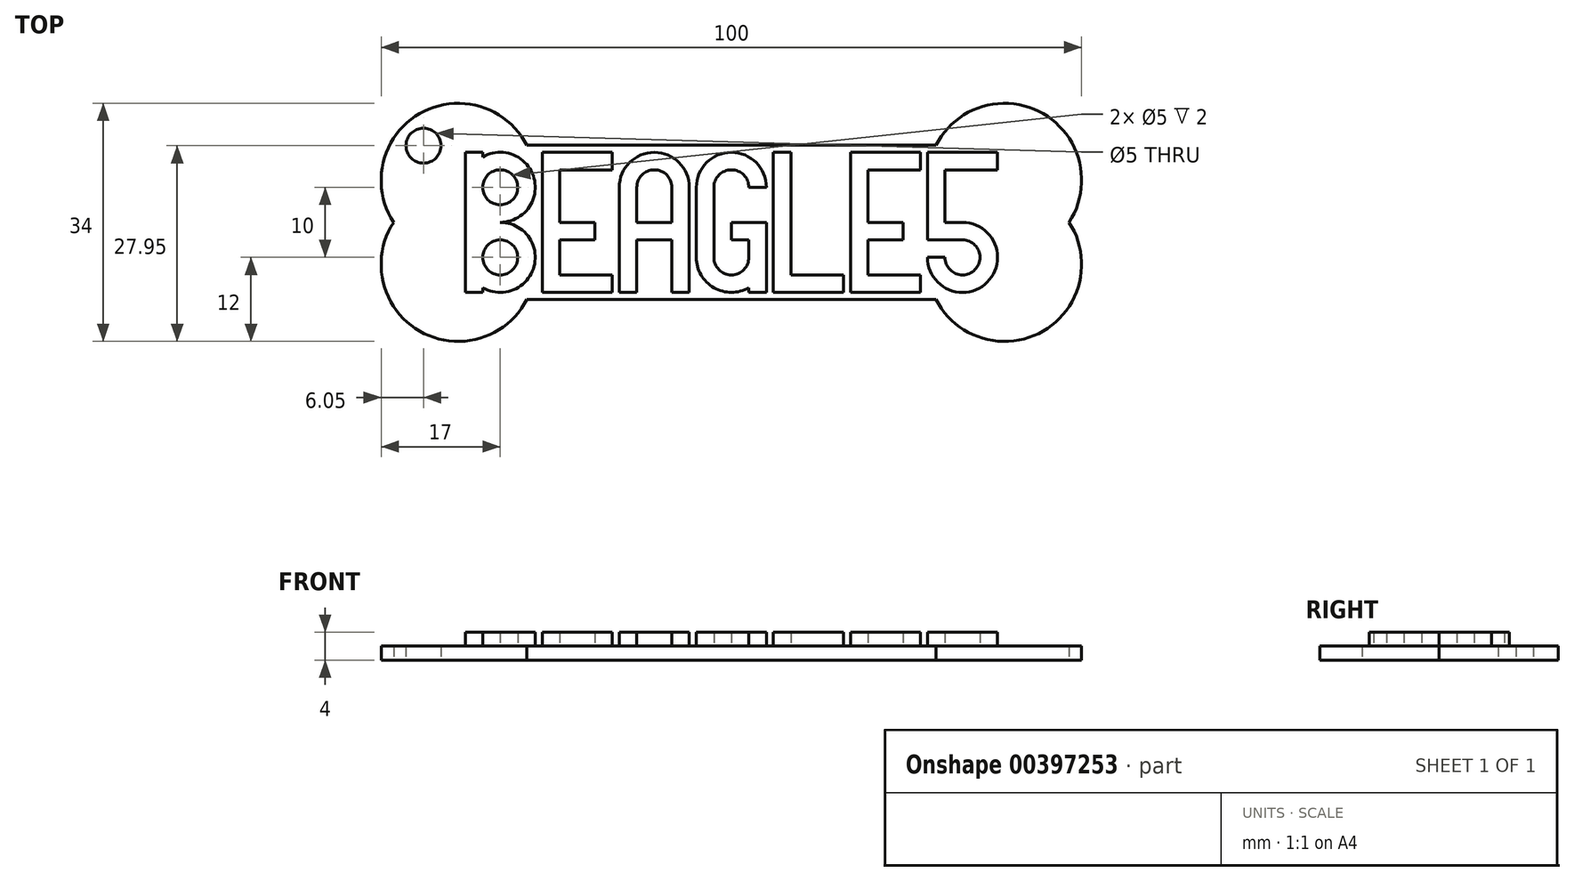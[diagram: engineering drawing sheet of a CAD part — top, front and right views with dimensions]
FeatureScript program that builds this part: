
annotation { "Feature Type Name" : "Feature", "Feature Type Description" : "" }
export const myFeature = defineFeature(function(context is Context, id is Id, definition is map)
    precondition{}
    {
        {
            var Q0;
            Q0=qCreatedBy(makeId("Top.planeOp"),FACE);
            var sketch = newSketch(context, id + "F0", { "sketchPlane" : qUnion([Q0])});
            skLineSegment(sketch, "E0.bottom", {"start": v(0, 0) * mm, "end": v(-78, 0) * mm});
            skLineSegment(sketch, "E0.top", {"start": v(0, 22) * mm, "end": v(-78, 22) * mm});
            skLineSegment(sketch, "E0.left", {"start": v(0, 0) * mm, "end": v(0, 22) * mm});
            skLineSegment(sketch, "E0.right", {"start": v(-78, 0) * mm, "end": v(-78, 22) * mm});
            skPoint(sketch, "E1", {"position": v(-78, 17) * mm});
            skPoint(sketch, "E2", {"position": v(-78, 5) * mm});
            skPoint(sketch, "E3", {"position": v(0, 5) * mm});
            skCircle(sketch, "E4", {"center": v(-78, 17) * mm, "radius": 11 * mm});
            skCircle(sketch, "E5", {"center": v(-78, 5) * mm, "radius": 11 * mm});
            skPoint(sketch, "E6", {"position": v(0, 17) * mm});
            skCircle(sketch, "E7", {"center": v(0, 17) * mm, "radius": 11 * mm});
            skCircle(sketch, "E8", {"center": v(0, 5) * mm, "radius": 11 * mm});
            skLineSegment(sketch, "E9", {"start": v(-78, 17) * mm, "end": v(-89, 17) * mm, "construction": true});
            skLineSegment(sketch, "E10", {"start": v(-78, 17) * mm, "end": v(-85.78, 24.78) * mm, "construction": true});
            skCircle(sketch, "E11", {"center": v(-82.95, 21.95) * mm, "radius": 2.5 * mm});
            skSolve(sketch);
        }
        {
            var Q0;
            Q0 = qSketchRegion(id + "F0", true);
            var Q1;
            {var subQ0=sQuery(id+"F0.wireOp",EDGE,"E4");var subQ1=sQuery(id+"F0.wireOp",EDGE,"E0.right");var subQ2=makeQuery(id+"F0.imprint","INTERSECT",VERTEX,{"derivedFrom":[subQ1,subQ0]});Q1=makeQuery(id+"F0.imprint","IMPRINT",FACE,{"disambiguationData":[TD([[makeQuery(id+"F0.imprint","IMPRINT",EDGE,{"disambiguationData":[TD([[subQ2,-1.0]])],"derivedFrom":subQ1}),-1.0]])]});}
            var Q2;
            {var subQ0=sQuery(id+"F0.wireOp",EDGE,"E7");var subQ1=sQuery(id+"F0.wireOp",EDGE,"E0.left");var subQ2=makeQuery(id+"F0.imprint","INTERSECT",VERTEX,{"derivedFrom":[subQ1,subQ0]});Q2=makeQuery(id+"F0.imprint","IMPRINT",FACE,{"disambiguationData":[TD([[makeQuery(id+"F0.imprint","IMPRINT",EDGE,{"disambiguationData":[TD([[subQ2,-1.0]])],"derivedFrom":subQ1}),1.0]])]});}
            extrude(context, id + "F1", {"entities" : qUnion([Q0, Q1, Q2]), "depth" : 2 * mm});
        }
        {
            var Q0;
            Q0=makeQuery(id+"F1.opExtrude","CAP_FACE",FACE,{"disambiguationData":[OSD([sQuery(id+"F0.wireOp",EDGE,"E0.bottom"),sQuery(id+"F0.wireOp",EDGE,"E0.top"),sQuery(id+"F0.wireOp",EDGE,"E4"),sQuery(id+"F0.wireOp",EDGE,"E5"),sQuery(id+"F0.wireOp",EDGE,"E7"),sQuery(id+"F0.wireOp",EDGE,"E8"),sQuery(id+"F0.wireOp",EDGE,"E11")])],"isStart":false});
            var sketch = newSketch(context, id + "F2", { "sketchPlane" : qUnion([Q0])});
            skLineSegment(sketch, "E12.bottom", {"start": v(0, 0) * mm, "end": v(-78, 0) * mm, "construction": true});
            skLineSegment(sketch, "E12.top", {"start": v(0, 22) * mm, "end": v(-78, 22) * mm, "construction": true});
            skLineSegment(sketch, "E12.left", {"start": v(0, 0) * mm, "end": v(0, 22) * mm, "construction": true});
            skLineSegment(sketch, "E12.right", {"start": v(-78, 0) * mm, "end": v(-78, 22) * mm, "construction": true});
            skLineSegment(sketch, "E13.bottom", {"start": v(-77, 21) * mm, "end": v(-67, 21) * mm, "construction": true});
            skLineSegment(sketch, "E13.top", {"start": v(-77, 1) * mm, "end": v(-67, 1) * mm, "construction": true});
            skLineSegment(sketch, "E13.left", {"start": v(-77, 21) * mm, "end": v(-77, 1) * mm, "construction": true});
            skLineSegment(sketch, "E13.right", {"start": v(-67, 21) * mm, "end": v(-67, 1) * mm, "construction": true});
            skLineSegment(sketch, "E14", {"start": v(-77, 11) * mm, "end": v(-67, 11) * mm, "construction": true});
            skLineSegment(sketch, "E15.bottom", {"start": v(-22, 21) * mm, "end": v(-12, 21) * mm, "construction": true});
            skLineSegment(sketch, "E15.top", {"start": v(-22, 1) * mm, "end": v(-12, 1) * mm, "construction": true});
            skLineSegment(sketch, "E15.left", {"start": v(-22, 21) * mm, "end": v(-22, 1) * mm, "construction": true});
            skLineSegment(sketch, "E15.right", {"start": v(-12, 21) * mm, "end": v(-12, 1) * mm, "construction": true});
            skLineSegment(sketch, "E16", {"start": v(-22, 11) * mm, "end": v(-12, 11) * mm, "construction": true});
            skLineSegment(sketch, "E17.bottom", {"start": v(-55, 21) * mm, "end": v(-45, 21) * mm, "construction": true});
            skLineSegment(sketch, "E17.top", {"start": v(-55, 1) * mm, "end": v(-45, 1) * mm, "construction": true});
            skLineSegment(sketch, "E17.left", {"start": v(-55, 21) * mm, "end": v(-55, 1) * mm, "construction": true});
            skLineSegment(sketch, "E17.right", {"start": v(-45, 21) * mm, "end": v(-45, 1) * mm, "construction": true});
            skLineSegment(sketch, "E18", {"start": v(-55, 11) * mm, "end": v(-45, 11) * mm, "construction": true});
            skLineSegment(sketch, "E19.bottom", {"start": v(-33, 21) * mm, "end": v(-23, 21) * mm, "construction": true});
            skLineSegment(sketch, "E19.top", {"start": v(-33, 1) * mm, "end": v(-23, 1) * mm, "construction": true});
            skLineSegment(sketch, "E19.left", {"start": v(-33, 21) * mm, "end": v(-33, 1) * mm, "construction": true});
            skLineSegment(sketch, "E19.right", {"start": v(-23, 21) * mm, "end": v(-23, 1) * mm, "construction": true});
            skLineSegment(sketch, "E20", {"start": v(-28, 21) * mm, "end": v(-28, 1) * mm, "construction": true});
            skLineSegment(sketch, "E21", {"start": v(-33, 11) * mm, "end": v(-23, 11) * mm, "construction": true});
            skLineSegment(sketch, "E22.bottom", {"start": v(-11, 21) * mm, "end": v(-1, 21) * mm, "construction": true});
            skLineSegment(sketch, "E22.top", {"start": v(-11, 1) * mm, "end": v(-1, 1) * mm, "construction": true});
            skLineSegment(sketch, "E22.left", {"start": v(-11, 21) * mm, "end": v(-11, 1) * mm, "construction": true});
            skLineSegment(sketch, "E22.right", {"start": v(-1, 21) * mm, "end": v(-1, 1) * mm, "construction": true});
            skLineSegment(sketch, "E23", {"start": v(-6, 21) * mm, "end": v(-6, 1) * mm, "construction": true});
            skLineSegment(sketch, "E24", {"start": v(-11, 11) * mm, "end": v(-1, 11) * mm, "construction": true});
            skLineSegment(sketch, "E25", {"start": v(-77, 21) * mm, "end": v(-67, 11) * mm, "construction": true});
            skLineSegment(sketch, "E26", {"start": v(-77, 11) * mm, "end": v(-67, 21) * mm, "construction": true});
            skLineSegment(sketch, "E27", {"start": v(-77, 11) * mm, "end": v(-67, 1) * mm, "construction": true});
            skLineSegment(sketch, "E28", {"start": v(-77, 1) * mm, "end": v(-67, 11) * mm, "construction": true});
            skCircle(sketch, "E29", {"center": v(-72, 16) * mm, "radius": 5 * mm});
            skCircle(sketch, "E30", {"center": v(-72, 6) * mm, "radius": 5 * mm});
            skLineSegment(sketch, "E31", {"start": v(-74.5, 21) * mm, "end": v(-74.5, 1) * mm});
            skCircle(sketch, "E32", {"center": v(-72, 16) * mm, "radius": 2.5 * mm});
            skCircle(sketch, "E33", {"center": v(-72, 6) * mm, "radius": 2.5 * mm});
            skLineSegment(sketch, "E34", {"start": v(-77, 21) * mm, "end": v(-74.5, 21) * mm});
            skLineSegment(sketch, "E35", {"start": v(-77, 21) * mm, "end": v(-77, 1) * mm});
            skLineSegment(sketch, "E36", {"start": v(-77, 1) * mm, "end": v(-74.5, 1) * mm});
            skLineSegment(sketch, "E37", {"start": v(-22, 21) * mm, "end": v(-22, 1) * mm});
            skLineSegment(sketch, "E38", {"start": v(-19.5, 1) * mm, "end": v(-19.5, 21) * mm});
            skLineSegment(sketch, "E39", {"start": v(-22, 18.5) * mm, "end": v(-12, 18.5) * mm});
            skLineSegment(sketch, "E40", {"start": v(-22, 3.5) * mm, "end": v(-12, 3.5) * mm});
            skLineSegment(sketch, "E41", {"start": v(-22, 11) * mm, "end": v(-12, 11) * mm});
            skLineSegment(sketch, "E42", {"start": v(-22, 8.5) * mm, "end": v(-12, 8.5) * mm});
            skLineSegment(sketch, "E43", {"start": v(-14.5, 11) * mm, "end": v(-14.5, 8.5) * mm});
            skLineSegment(sketch, "E44", {"start": v(-22, 21) * mm, "end": v(-12, 21) * mm});
            skLineSegment(sketch, "E45", {"start": v(-22, 1) * mm, "end": v(-12, 1) * mm});
            skLineSegment(sketch, "E46", {"start": v(-12, 21) * mm, "end": v(-12, 18.5) * mm});
            skLineSegment(sketch, "E47", {"start": v(-12, 3.5) * mm, "end": v(-12, 1) * mm});
            skLineSegment(sketch, "E48", {"start": v(-55, 21) * mm, "end": v(-45, 11) * mm, "construction": true});
            skLineSegment(sketch, "E49", {"start": v(-45, 21) * mm, "end": v(-55, 11) * mm, "construction": true});
            skLineSegment(sketch, "E50", {"start": v(-55, 21) * mm, "end": v(-55, 1) * mm});
            skLineSegment(sketch, "E51", {"start": v(-45, 21) * mm, "end": v(-45, 1) * mm});
            skLineSegment(sketch, "E52", {"start": v(-55, 11) * mm, "end": v(-45, 11) * mm});
            skLineSegment(sketch, "E53", {"start": v(-55, 8.5) * mm, "end": v(-45, 8.5) * mm});
            skLineSegment(sketch, "E54", {"start": v(-52.5, 21) * mm, "end": v(-52.5, 1) * mm});
            skLineSegment(sketch, "E55", {"start": v(-47.5, 21) * mm, "end": v(-47.5, 1) * mm});
            skLineSegment(sketch, "E56", {"start": v(-55, 1) * mm, "end": v(-52.5, 1) * mm});
            skLineSegment(sketch, "E57", {"start": v(-47.5, 1) * mm, "end": v(-45, 1) * mm});
            skCircle(sketch, "E58", {"center": v(-50, 16) * mm, "radius": 5 * mm});
            skCircle(sketch, "E59", {"center": v(-50, 16) * mm, "radius": 2.5 * mm});
            skLineSegment(sketch, "E60", {"start": v(-30.5, 21) * mm, "end": v(-30.5, 1) * mm});
            skLineSegment(sketch, "E61", {"start": v(-33, 21) * mm, "end": v(-33, 1) * mm});
            skLineSegment(sketch, "E62", {"start": v(-33, 21) * mm, "end": v(-30.5, 21) * mm});
            skLineSegment(sketch, "E63", {"start": v(-33, 1) * mm, "end": v(-30.5, 1) * mm});
            skLineSegment(sketch, "E64", {"start": v(-33, 3.5) * mm, "end": v(-23, 3.5) * mm});
            skLineSegment(sketch, "E65", {"start": v(-23, 3.5) * mm, "end": v(-23, 1) * mm});
            skLineSegment(sketch, "E66", {"start": v(-33, 1) * mm, "end": v(-23, 1) * mm});
            skLineSegment(sketch, "E67", {"start": v(-11, 21) * mm, "end": v(-1, 21) * mm});
            skLineSegment(sketch, "E68", {"start": v(-11, 21) * mm, "end": v(-11, 1) * mm});
            skLineSegment(sketch, "E69", {"start": v(-11, 11) * mm, "end": v(-1, 11) * mm});
            skLineSegment(sketch, "E70", {"start": v(-11, 11) * mm, "end": v(-1, 1) * mm, "construction": true});
            skLineSegment(sketch, "E71", {"start": v(-1, 11) * mm, "end": v(-11, 1) * mm, "construction": true});
            skCircle(sketch, "E72", {"center": v(-6, 6) * mm, "radius": 5 * mm});
            skLineSegment(sketch, "E73.bottom", {"start": v(-66, 21) * mm, "end": v(-56, 21) * mm, "construction": true});
            skLineSegment(sketch, "E73.top", {"start": v(-66, 1) * mm, "end": v(-56, 1) * mm, "construction": true});
            skLineSegment(sketch, "E73.left", {"start": v(-66, 21) * mm, "end": v(-66, 1) * mm, "construction": true});
            skLineSegment(sketch, "E73.right", {"start": v(-56, 21) * mm, "end": v(-56, 1) * mm, "construction": true});
            skLineSegment(sketch, "E74", {"start": v(-66, 11) * mm, "end": v(-56, 11) * mm, "construction": true});
            skLineSegment(sketch, "E75", {"start": v(-66, 21) * mm, "end": v(-66, 1) * mm});
            skLineSegment(sketch, "E76", {"start": v(-63.5, 1) * mm, "end": v(-63.5, 21) * mm});
            skLineSegment(sketch, "E77", {"start": v(-66, 18.5) * mm, "end": v(-56, 18.5) * mm});
            skLineSegment(sketch, "E78", {"start": v(-66, 3.5) * mm, "end": v(-56, 3.5) * mm});
            skLineSegment(sketch, "E79", {"start": v(-66, 11) * mm, "end": v(-56, 11) * mm});
            skLineSegment(sketch, "E80", {"start": v(-66, 8.5) * mm, "end": v(-56, 8.5) * mm});
            skLineSegment(sketch, "E81", {"start": v(-58.5, 11) * mm, "end": v(-58.5, 8.5) * mm});
            skLineSegment(sketch, "E82", {"start": v(-66, 21) * mm, "end": v(-56, 21) * mm});
            skLineSegment(sketch, "E83", {"start": v(-66, 1) * mm, "end": v(-56, 1) * mm});
            skLineSegment(sketch, "E84", {"start": v(-56, 21) * mm, "end": v(-56, 18.5) * mm});
            skLineSegment(sketch, "E85", {"start": v(-56, 3.5) * mm, "end": v(-56, 1) * mm});
            skLineSegment(sketch, "E86.bottom", {"start": v(-44, 21) * mm, "end": v(-34, 21) * mm, "construction": true});
            skLineSegment(sketch, "E86.top", {"start": v(-44, 1) * mm, "end": v(-34, 1) * mm, "construction": true});
            skLineSegment(sketch, "E86.left", {"start": v(-44, 21) * mm, "end": v(-44, 1) * mm, "construction": true});
            skLineSegment(sketch, "E86.right", {"start": v(-34, 21) * mm, "end": v(-34, 1) * mm, "construction": true});
            skLineSegment(sketch, "E87", {"start": v(-44, 11) * mm, "end": v(-34, 11) * mm, "construction": true});
            skLineSegment(sketch, "E88", {"start": v(-44, 21) * mm, "end": v(-34, 11) * mm, "construction": true});
            skLineSegment(sketch, "E89", {"start": v(-44, 11) * mm, "end": v(-34, 21) * mm, "construction": true});
            skLineSegment(sketch, "E90", {"start": v(-44, 11) * mm, "end": v(-34, 1) * mm, "construction": true});
            skLineSegment(sketch, "E91", {"start": v(-44, 1) * mm, "end": v(-34, 11) * mm, "construction": true});
            skCircle(sketch, "E92", {"center": v(-39, 16) * mm, "radius": 5 * mm});
            skCircle(sketch, "E93", {"center": v(-39, 6) * mm, "radius": 5 * mm});
            skLineSegment(sketch, "E94", {"start": v(-41.5, 21) * mm, "end": v(-41.5, 1) * mm});
            skCircle(sketch, "E95", {"center": v(-39, 6) * mm, "radius": 2.5 * mm});
            skLineSegment(sketch, "E96", {"start": v(-44, 21) * mm, "end": v(-41.5, 21) * mm});
            skLineSegment(sketch, "E97", {"start": v(-44, 21) * mm, "end": v(-44, 1) * mm});
            skLineSegment(sketch, "E98", {"start": v(-44, 1) * mm, "end": v(-41.5, 1) * mm});
            skLineSegment(sketch, "E99", {"start": v(-36.5, 21) * mm, "end": v(-36.5, 1) * mm});
            skLineSegment(sketch, "E100", {"start": v(-34, 11) * mm, "end": v(-34, 1) * mm});
            skLineSegment(sketch, "E101", {"start": v(-36.5, 11) * mm, "end": v(-34, 11) * mm});
            skLineSegment(sketch, "E102", {"start": v(-44, 11) * mm, "end": v(-34, 11) * mm});
            skLineSegment(sketch, "E103", {"start": v(-44, 8.5) * mm, "end": v(-34, 8.5) * mm});
            skCircle(sketch, "E104", {"center": v(-39, 16) * mm, "radius": 2.5 * mm});
            skLineSegment(sketch, "E105", {"start": v(-36.5, 16) * mm, "end": v(-34, 16) * mm});
            skLineSegment(sketch, "E106", {"start": v(-36.5, 1) * mm, "end": v(-34, 1) * mm});
            skLineSegment(sketch, "E107", {"start": v(-39, 8.5) * mm, "end": v(-39, 11) * mm});
            skLineSegment(sketch, "E108", {"start": v(-1, 18.5) * mm, "end": v(-11, 18.5) * mm});
            skLineSegment(sketch, "E109", {"start": v(-1, 21) * mm, "end": v(-1, 18.5) * mm});
            skLineSegment(sketch, "E110", {"start": v(-8.5, 21) * mm, "end": v(-8.5, 11) * mm});
            skLineSegment(sketch, "E111", {"start": v(-11, 8.5) * mm, "end": v(-1, 8.5) * mm});
            skCircle(sketch, "E112", {"center": v(-6, 6) * mm, "radius": 2.5 * mm});
            skLineSegment(sketch, "E113", {"start": v(-8.5, 6) * mm, "end": v(-11, 6) * mm});
            skSolve(sketch);
        }
        {
            var Q0;
            {var subQ0=sQuery(id+"F2.wireOp",EDGE,"E109");Q0=makeQuery(id+"F2.imprint","IMPRINT",FACE,{"disambiguationData":[TD([[makeQuery(id+"F2.imprint","IMPRINT",EDGE,{"derivedFrom":subQ0}),-1.0]])]});}
            var Q1;
            {var subQ0=sQuery(id+"F2.wireOp",EDGE,"E68");var subQ1=sQuery(id+"F2.wireOp",EDGE,"E67");var subQ2=makeQuery(id+"F2.imprint","INTERSECT",VERTEX,{"derivedFrom":[subQ1,subQ0]});Q1=makeQuery(id+"F2.imprint","IMPRINT",FACE,{"disambiguationData":[TD([[makeQuery(id+"F2.imprint","IMPRINT",EDGE,{"disambiguationData":[TD([[subQ2,-1.0]])],"derivedFrom":subQ1}),-1.0]])]});}
            var Q2;
            {var subQ0=sQuery(id+"F2.wireOp",EDGE,"E69");var subQ1=sQuery(id+"F2.wireOp",EDGE,"E68");var subQ2=makeQuery(id+"F2.imprint","INTERSECT",VERTEX,{"derivedFrom":[subQ1,subQ0]});Q2=makeQuery(id+"F2.imprint","IMPRINT",FACE,{"disambiguationData":[TD([[makeQuery(id+"F2.imprint","IMPRINT",EDGE,{"disambiguationData":[TD([[subQ2,1.0]])],"derivedFrom":subQ1}),1.0]])]});}
            var Q3;
            {var subQ0=sQuery(id+"F2.wireOp",EDGE,"E69");var subQ4=sQuery(id+"F2.wireOp",EDGE,"E68");var subQ5=makeQuery(id+"F2.imprint","INTERSECT",VERTEX,{"derivedFrom":[subQ4,subQ0]});Q3=makeQuery(id+"F2.imprint","IMPRINT",FACE,{"disambiguationData":[TD([[makeQuery(id+"F2.imprint","IMPRINT",EDGE,{"disambiguationData":[TD([[subQ5,-1.0]])],"derivedFrom":subQ4}),1.0]])]});}
            var Q4;
            {var subQ0=sQuery(id+"F2.wireOp",EDGE,"E72");var subQ1=makeQuery(id+"F2.imprint","INTERSECT",VERTEX,{"derivedFrom":[sQuery(id+"F2.wireOp",EDGE,"E69"),subQ0]});Q4=makeQuery(id+"F2.imprint","IMPRINT",FACE,{"disambiguationData":[TD([[makeQuery(id+"F2.imprint","IMPRINT",EDGE,{"disambiguationData":[TD([[subQ1,1.0]])],"derivedFrom":subQ0}),1.0]])]});}
            var Q5;
            {var subQ0=sQuery(id+"F2.wireOp",EDGE,"E113");Q5=makeQuery(id+"F2.imprint","IMPRINT",FACE,{"disambiguationData":[TD([[makeQuery(id+"F2.imprint","IMPRINT",EDGE,{"derivedFrom":subQ0}),1.0]])]});}
            var Q6;
            {var subQ5=sQuery(id+"F2.wireOp",EDGE,"E43");Q6=makeQuery(id+"F2.imprint","IMPRINT",FACE,{"disambiguationData":[TD([[makeQuery(id+"F2.imprint","IMPRINT",EDGE,{"derivedFrom":subQ5}),-1.0]])]});}
            var Q7;
            {var subQ0=sQuery(id+"F2.wireOp",EDGE,"E41");var subQ1=sQuery(id+"F2.wireOp",EDGE,"E37");var subQ2=makeQuery(id+"F2.imprint","INTERSECT",VERTEX,{"derivedFrom":[subQ1,subQ0]});Q7=makeQuery(id+"F2.imprint","IMPRINT",FACE,{"disambiguationData":[TD([[makeQuery(id+"F2.imprint","IMPRINT",EDGE,{"disambiguationData":[TD([[subQ2,-1.0]])],"derivedFrom":subQ1}),1.0]])]});}
            var Q8;
            {var subQ0=sQuery(id+"F2.wireOp",EDGE,"E39");var subQ1=sQuery(id+"F2.wireOp",EDGE,"E37");var subQ2=makeQuery(id+"F2.imprint","INTERSECT",VERTEX,{"derivedFrom":[subQ1,subQ0]});Q8=makeQuery(id+"F2.imprint","IMPRINT",FACE,{"disambiguationData":[TD([[makeQuery(id+"F2.imprint","IMPRINT",EDGE,{"disambiguationData":[TD([[subQ2,-1.0]])],"derivedFrom":subQ1}),1.0]])]});}
            var Q9;
            {var subQ0=sQuery(id+"F2.wireOp",EDGE,"E44");var subQ1=sQuery(id+"F2.wireOp",EDGE,"E37");var subQ2=makeQuery(id+"F2.imprint","INTERSECT",VERTEX,{"derivedFrom":[subQ1,subQ0]});Q9=makeQuery(id+"F2.imprint","IMPRINT",FACE,{"disambiguationData":[TD([[makeQuery(id+"F2.imprint","IMPRINT",EDGE,{"disambiguationData":[TD([[subQ2,-1.0]])],"derivedFrom":subQ1}),1.0]])]});}
            var Q10;
            {var subQ5=sQuery(id+"F2.wireOp",EDGE,"E46");Q10=makeQuery(id+"F2.imprint","IMPRINT",FACE,{"disambiguationData":[TD([[makeQuery(id+"F2.imprint","IMPRINT",EDGE,{"derivedFrom":subQ5}),-1.0]])]});}
            var Q11;
            {var subQ0=sQuery(id+"F2.wireOp",EDGE,"E40");var subQ1=sQuery(id+"F2.wireOp",EDGE,"E37");var subQ2=makeQuery(id+"F2.imprint","INTERSECT",VERTEX,{"derivedFrom":[subQ1,subQ0]});Q11=makeQuery(id+"F2.imprint","IMPRINT",FACE,{"disambiguationData":[TD([[makeQuery(id+"F2.imprint","IMPRINT",EDGE,{"disambiguationData":[TD([[subQ2,1.0]])],"derivedFrom":subQ1}),1.0]])]});}
            var Q12;
            {var subQ0=sQuery(id+"F2.wireOp",EDGE,"E45");var subQ1=sQuery(id+"F2.wireOp",EDGE,"E37");var subQ2=makeQuery(id+"F2.imprint","INTERSECT",VERTEX,{"derivedFrom":[subQ1,subQ0]});Q12=makeQuery(id+"F2.imprint","IMPRINT",FACE,{"disambiguationData":[TD([[makeQuery(id+"F2.imprint","IMPRINT",EDGE,{"disambiguationData":[TD([[subQ2,1.0]])],"derivedFrom":subQ1}),1.0]])]});}
            var Q13;
            {var subQ5=sQuery(id+"F2.wireOp",EDGE,"E47");Q13=makeQuery(id+"F2.imprint","IMPRINT",FACE,{"disambiguationData":[TD([[makeQuery(id+"F2.imprint","IMPRINT",EDGE,{"derivedFrom":subQ5}),-1.0]])]});}
            var Q14;
            {var subQ5=sQuery(id+"F2.wireOp",EDGE,"E65");Q14=makeQuery(id+"F2.imprint","IMPRINT",FACE,{"disambiguationData":[TD([[makeQuery(id+"F2.imprint","IMPRINT",EDGE,{"derivedFrom":subQ5}),-1.0]])]});}
            var Q15;
            {var subQ0=sQuery(id+"F2.wireOp",EDGE,"E66");var subQ1=sQuery(id+"F2.wireOp",EDGE,"E60");var subQ2=makeQuery(id+"F2.imprint","INTERSECT",VERTEX,{"derivedFrom":[subQ1,subQ0]});Q15=makeQuery(id+"F2.imprint","IMPRINT",FACE,{"disambiguationData":[TD([[makeQuery(id+"F2.imprint","IMPRINT",EDGE,{"disambiguationData":[TD([[subQ2,1.0]])],"derivedFrom":subQ1}),-1.0]])]});}
            var Q16;
            {var subQ0=sQuery(id+"F2.wireOp",EDGE,"E62");Q16=makeQuery(id+"F2.imprint","IMPRINT",FACE,{"disambiguationData":[TD([[makeQuery(id+"F2.imprint","IMPRINT",EDGE,{"derivedFrom":subQ0}),-1.0]])]});}
            var Q17;
            {var subQ0=sQuery(id+"F2.wireOp",EDGE,"E94");var subQ1=sQuery(id+"F2.wireOp",EDGE,"E92");var subQ2=makeQuery(id+"F2.imprint","INTERSECT",VERTEX,{"disambiguationData":[OD(0.0)],"derivedFrom":[subQ1,subQ0]});Q17=makeQuery(id+"F2.imprint","IMPRINT",FACE,{"disambiguationData":[TD([[makeQuery(id+"F2.imprint","IMPRINT",EDGE,{"disambiguationData":[TD([[subQ2,-1.0]])],"derivedFrom":subQ1}),1.0]])]});}
            var Q18;
            {var subQ0=sQuery(id+"F2.wireOp",EDGE,"E97");var subQ1=sQuery(id+"F2.wireOp",EDGE,"E92");var subQ2=makeQuery(id+"F2.imprint","INTERSECT",VERTEX,{"derivedFrom":[subQ1,subQ0]});Q18=makeQuery(id+"F2.imprint","IMPRINT",FACE,{"disambiguationData":[TD([[makeQuery(id+"F2.imprint","IMPRINT",EDGE,{"disambiguationData":[TD([[subQ2,-1.0]])],"derivedFrom":subQ1}),-1.0]])]});}
            var Q19;
            {var subQ0=sQuery(id+"F2.wireOp",EDGE,"E94");var subQ1=sQuery(id+"F2.wireOp",EDGE,"E93");var subQ2=makeQuery(id+"F2.imprint","INTERSECT",VERTEX,{"disambiguationData":[OD(0.0)],"derivedFrom":[subQ1,subQ0]});Q19=makeQuery(id+"F2.imprint","IMPRINT",FACE,{"disambiguationData":[TD([[makeQuery(id+"F2.imprint","IMPRINT",EDGE,{"disambiguationData":[TD([[subQ2,-1.0]])],"derivedFrom":subQ1}),-1.0]])]});}
            var Q20;
            {var subQ1=sQuery(id+"F2.wireOp",EDGE,"E93");var subQ4=sQuery(id+"F2.wireOp",EDGE,"E103");var subQ5=makeQuery(id+"F2.imprint","INTERSECT",VERTEX,{"disambiguationData":[OD(1.0)],"derivedFrom":[subQ1,subQ4]});Q20=makeQuery(id+"F2.imprint","IMPRINT",FACE,{"disambiguationData":[TD([[makeQuery(id+"F2.imprint","IMPRINT",EDGE,{"disambiguationData":[TD([[subQ5,-1.0]])],"derivedFrom":subQ1}),1.0]])]});}
            var Q21;
            {var subQ0=sQuery(id+"F2.wireOp",EDGE,"E103");var subQ1=sQuery(id+"F2.wireOp",EDGE,"E93");var subQ2=makeQuery(id+"F2.imprint","INTERSECT",VERTEX,{"disambiguationData":[OD(1.0)],"derivedFrom":[subQ1,subQ0]});Q21=makeQuery(id+"F2.imprint","IMPRINT",FACE,{"disambiguationData":[TD([[makeQuery(id+"F2.imprint","IMPRINT",EDGE,{"disambiguationData":[TD([[subQ2,-1.0]])],"derivedFrom":subQ1}),-1.0]])]});}
            var Q22;
            {var subQ0=sQuery(id+"F2.wireOp",EDGE,"E94");var subQ1=sQuery(id+"F2.wireOp",EDGE,"E93");var subQ2=makeQuery(id+"F2.imprint","INTERSECT",VERTEX,{"disambiguationData":[OD(0.0)],"derivedFrom":[subQ1,subQ0]});Q22=makeQuery(id+"F2.imprint","IMPRINT",FACE,{"disambiguationData":[TD([[makeQuery(id+"F2.imprint","IMPRINT",EDGE,{"disambiguationData":[TD([[subQ2,-1.0]])],"derivedFrom":subQ1}),1.0]])]});}
            var Q23;
            {var subQ0=sQuery(id+"F2.wireOp",EDGE,"E107");Q23=makeQuery(id+"F2.imprint","IMPRINT",FACE,{"disambiguationData":[TD([[makeQuery(id+"F2.imprint","IMPRINT",EDGE,{"derivedFrom":subQ0}),-1.0]])]});}
            var Q24;
            {var subQ1=sQuery(id+"F2.wireOp",EDGE,"E93");var subQ3=sQuery(id+"F2.wireOp",EDGE,"E99");var subQ4=makeQuery(id+"F2.imprint","INTERSECT",VERTEX,{"disambiguationData":[OD(0.0)],"derivedFrom":[subQ1,subQ3]});Q24=makeQuery(id+"F2.imprint","IMPRINT",FACE,{"disambiguationData":[TD([[makeQuery(id+"F2.imprint","IMPRINT",EDGE,{"disambiguationData":[TD([[subQ4,1.0]])],"derivedFrom":subQ3}),-1.0]])]});}
            var Q25;
            {var subQ5=sQuery(id+"F2.wireOp",EDGE,"E93");var subQ7=sQuery(id+"F2.wireOp",EDGE,"E103");var subQ9=makeQuery(id+"F2.imprint","INTERSECT",VERTEX,{"disambiguationData":[OD(0.0)],"derivedFrom":[subQ5,subQ7]});Q25=makeQuery(id+"F2.imprint","IMPRINT",FACE,{"disambiguationData":[TD([[makeQuery(id+"F2.imprint","IMPRINT",EDGE,{"disambiguationData":[TD([[subQ9,-1.0]])],"derivedFrom":subQ5}),-1.0]])]});}
            var Q26;
            {var subQ0=sQuery(id+"F2.wireOp",EDGE,"E103");var subQ1=sQuery(id+"F2.wireOp",EDGE,"E93");var subQ2=makeQuery(id+"F2.imprint","INTERSECT",VERTEX,{"disambiguationData":[OD(0.0)],"derivedFrom":[subQ1,subQ0]});Q26=makeQuery(id+"F2.imprint","IMPRINT",FACE,{"disambiguationData":[TD([[makeQuery(id+"F2.imprint","IMPRINT",EDGE,{"disambiguationData":[TD([[subQ2,-1.0]])],"derivedFrom":subQ1}),1.0]])]});}
            var Q27;
            {var subQ1=sQuery(id+"F2.wireOp",EDGE,"E93");var subQ4=sQuery(id+"F2.wireOp",EDGE,"E103");var subQ6=makeQuery(id+"F2.imprint","INTERSECT",VERTEX,{"disambiguationData":[OD(0.0)],"derivedFrom":[subQ1,subQ4]});Q27=makeQuery(id+"F2.imprint","IMPRINT",FACE,{"disambiguationData":[TD([[makeQuery(id+"F2.imprint","IMPRINT",EDGE,{"disambiguationData":[TD([[subQ6,1.0]])],"derivedFrom":subQ1}),1.0]])]});}
            var Q28;
            {var subQ0=sQuery(id+"F2.wireOp",EDGE,"E103");var subQ1=sQuery(id+"F2.wireOp",EDGE,"E93");var subQ2=makeQuery(id+"F2.imprint","INTERSECT",VERTEX,{"disambiguationData":[OD(0.0)],"derivedFrom":[subQ1,subQ0]});Q28=makeQuery(id+"F2.imprint","IMPRINT",FACE,{"disambiguationData":[TD([[makeQuery(id+"F2.imprint","IMPRINT",EDGE,{"disambiguationData":[TD([[subQ2,1.0]])],"derivedFrom":subQ1}),-1.0]])]});}
            var Q29;
            {var subQ5=sQuery(id+"F2.wireOp",EDGE,"E106");Q29=makeQuery(id+"F2.imprint","IMPRINT",FACE,{"disambiguationData":[TD([[makeQuery(id+"F2.imprint","IMPRINT",EDGE,{"derivedFrom":subQ5}),1.0]])]});}
            var Q30;
            {var subQ0=sQuery(id+"F2.wireOp",EDGE,"E94");var subQ1=sQuery(id+"F2.wireOp",EDGE,"E93");var subQ2=makeQuery(id+"F2.imprint","INTERSECT",VERTEX,{"disambiguationData":[OD(1.0)],"derivedFrom":[subQ1,subQ0]});Q30=makeQuery(id+"F2.imprint","IMPRINT",FACE,{"disambiguationData":[TD([[makeQuery(id+"F2.imprint","IMPRINT",EDGE,{"disambiguationData":[TD([[subQ2,-1.0]])],"derivedFrom":subQ1}),1.0]])]});}
            var Q31;
            {var subQ0=sQuery(id+"F2.wireOp",EDGE,"E105");Q31=makeQuery(id+"F2.imprint","IMPRINT",FACE,{"disambiguationData":[TD([[makeQuery(id+"F2.imprint","IMPRINT",EDGE,{"derivedFrom":subQ0}),1.0]])]});}
            var Q32;
            {var subQ0=sQuery(id+"F2.wireOp",EDGE,"E99");var subQ1=sQuery(id+"F2.wireOp",EDGE,"E92");var subQ2=makeQuery(id+"F2.imprint","INTERSECT",VERTEX,{"disambiguationData":[OD(0.0)],"derivedFrom":[subQ1,subQ0]});Q32=makeQuery(id+"F2.imprint","IMPRINT",FACE,{"disambiguationData":[TD([[makeQuery(id+"F2.imprint","IMPRINT",EDGE,{"disambiguationData":[TD([[subQ2,-1.0]])],"derivedFrom":subQ1}),1.0]])]});}
            var Q33;
            {var subQ0=sQuery(id+"F2.wireOp",EDGE,"E58");var subQ1=sQuery(id+"F2.wireOp",EDGE,"E54");var subQ2=makeQuery(id+"F2.imprint","INTERSECT",VERTEX,{"disambiguationData":[OD(0.0)],"derivedFrom":[subQ1,subQ0]});Q33=makeQuery(id+"F2.imprint","IMPRINT",FACE,{"disambiguationData":[TD([[makeQuery(id+"F2.imprint","IMPRINT",EDGE,{"disambiguationData":[TD([[subQ2,-1.0]])],"derivedFrom":subQ1}),-1.0]])]});}
            var Q34;
            {var subQ0=sQuery(id+"F2.wireOp",EDGE,"E52");var subQ1=sQuery(id+"F2.wireOp",EDGE,"E50");var subQ2=makeQuery(id+"F2.imprint","INTERSECT",VERTEX,{"derivedFrom":[subQ1,subQ0]});Q34=makeQuery(id+"F2.imprint","IMPRINT",FACE,{"disambiguationData":[TD([[makeQuery(id+"F2.imprint","IMPRINT",EDGE,{"disambiguationData":[TD([[subQ2,1.0]])],"derivedFrom":subQ1}),1.0]])]});}
            var Q35;
            {var subQ0=sQuery(id+"F2.wireOp",EDGE,"E52");var subQ1=sQuery(id+"F2.wireOp",EDGE,"E50");var subQ2=makeQuery(id+"F2.imprint","INTERSECT",VERTEX,{"derivedFrom":[subQ1,subQ0]});Q35=makeQuery(id+"F2.imprint","IMPRINT",FACE,{"disambiguationData":[TD([[makeQuery(id+"F2.imprint","IMPRINT",EDGE,{"disambiguationData":[TD([[subQ2,-1.0]])],"derivedFrom":subQ1}),1.0]])]});}
            var Q36;
            {var subQ0=sQuery(id+"F2.wireOp",EDGE,"E56");Q36=makeQuery(id+"F2.imprint","IMPRINT",FACE,{"disambiguationData":[TD([[makeQuery(id+"F2.imprint","IMPRINT",EDGE,{"derivedFrom":subQ0}),1.0]])]});}
            var Q37;
            {var subQ0=sQuery(id+"F2.wireOp",EDGE,"E57");Q37=makeQuery(id+"F2.imprint","IMPRINT",FACE,{"disambiguationData":[TD([[makeQuery(id+"F2.imprint","IMPRINT",EDGE,{"derivedFrom":subQ0}),1.0]])]});}
            var Q38;
            {var subQ0=sQuery(id+"F2.wireOp",EDGE,"E52");var subQ1=sQuery(id+"F2.wireOp",EDGE,"E51");var subQ2=makeQuery(id+"F2.imprint","INTERSECT",VERTEX,{"derivedFrom":[subQ1,subQ0]});Q38=makeQuery(id+"F2.imprint","IMPRINT",FACE,{"disambiguationData":[TD([[makeQuery(id+"F2.imprint","IMPRINT",EDGE,{"disambiguationData":[TD([[subQ2,-1.0]])],"derivedFrom":subQ1}),-1.0]])]});}
            var Q39;
            {var subQ0=sQuery(id+"F2.wireOp",EDGE,"E52");var subQ1=sQuery(id+"F2.wireOp",EDGE,"E51");var subQ2=makeQuery(id+"F2.imprint","INTERSECT",VERTEX,{"derivedFrom":[subQ1,subQ0]});Q39=makeQuery(id+"F2.imprint","IMPRINT",FACE,{"disambiguationData":[TD([[makeQuery(id+"F2.imprint","IMPRINT",EDGE,{"disambiguationData":[TD([[subQ2,1.0]])],"derivedFrom":subQ1}),-1.0]])]});}
            var Q40;
            {var subQ0=sQuery(id+"F2.wireOp",EDGE,"E58");var subQ1=sQuery(id+"F2.wireOp",EDGE,"E55");var subQ2=makeQuery(id+"F2.imprint","INTERSECT",VERTEX,{"disambiguationData":[OD(0.0)],"derivedFrom":[subQ1,subQ0]});Q40=makeQuery(id+"F2.imprint","IMPRINT",FACE,{"disambiguationData":[TD([[makeQuery(id+"F2.imprint","IMPRINT",EDGE,{"disambiguationData":[TD([[subQ2,-1.0]])],"derivedFrom":subQ1}),1.0]])]});}
            var Q41;
            {var subQ0=sQuery(id+"F2.wireOp",EDGE,"E58");var subQ1=sQuery(id+"F2.wireOp",EDGE,"E54");var subQ2=makeQuery(id+"F2.imprint","INTERSECT",VERTEX,{"disambiguationData":[OD(0.0)],"derivedFrom":[subQ1,subQ0]});Q41=makeQuery(id+"F2.imprint","IMPRINT",FACE,{"disambiguationData":[TD([[makeQuery(id+"F2.imprint","IMPRINT",EDGE,{"disambiguationData":[TD([[subQ2,-1.0]])],"derivedFrom":subQ1}),1.0]])]});}
            var Q42;
            {var subQ0=sQuery(id+"F2.wireOp",EDGE,"E54");var subQ1=sQuery(id+"F2.wireOp",EDGE,"E52");var subQ2=makeQuery(id+"F2.imprint","INTERSECT",VERTEX,{"derivedFrom":[subQ1,subQ0]});Q42=makeQuery(id+"F2.imprint","IMPRINT",FACE,{"disambiguationData":[TD([[makeQuery(id+"F2.imprint","IMPRINT",EDGE,{"disambiguationData":[TD([[subQ2,-1.0]])],"derivedFrom":subQ1}),-1.0]])]});}
            var Q43;
            {var subQ5=sQuery(id+"F2.wireOp",EDGE,"E81");Q43=makeQuery(id+"F2.imprint","IMPRINT",FACE,{"disambiguationData":[TD([[makeQuery(id+"F2.imprint","IMPRINT",EDGE,{"derivedFrom":subQ5}),-1.0]])]});}
            var Q44;
            {var subQ0=sQuery(id+"F2.wireOp",EDGE,"E79");var subQ1=sQuery(id+"F2.wireOp",EDGE,"E75");var subQ2=makeQuery(id+"F2.imprint","INTERSECT",VERTEX,{"derivedFrom":[subQ1,subQ0]});Q44=makeQuery(id+"F2.imprint","IMPRINT",FACE,{"disambiguationData":[TD([[makeQuery(id+"F2.imprint","IMPRINT",EDGE,{"disambiguationData":[TD([[subQ2,-1.0]])],"derivedFrom":subQ1}),1.0]])]});}
            var Q45;
            {var subQ0=sQuery(id+"F2.wireOp",EDGE,"E77");var subQ1=sQuery(id+"F2.wireOp",EDGE,"E75");var subQ2=makeQuery(id+"F2.imprint","INTERSECT",VERTEX,{"derivedFrom":[subQ1,subQ0]});Q45=makeQuery(id+"F2.imprint","IMPRINT",FACE,{"disambiguationData":[TD([[makeQuery(id+"F2.imprint","IMPRINT",EDGE,{"disambiguationData":[TD([[subQ2,-1.0]])],"derivedFrom":subQ1}),1.0]])]});}
            var Q46;
            {var subQ0=sQuery(id+"F2.wireOp",EDGE,"E82");var subQ1=sQuery(id+"F2.wireOp",EDGE,"E75");var subQ2=makeQuery(id+"F2.imprint","INTERSECT",VERTEX,{"derivedFrom":[subQ1,subQ0]});Q46=makeQuery(id+"F2.imprint","IMPRINT",FACE,{"disambiguationData":[TD([[makeQuery(id+"F2.imprint","IMPRINT",EDGE,{"disambiguationData":[TD([[subQ2,-1.0]])],"derivedFrom":subQ1}),1.0]])]});}
            var Q47;
            {var subQ5=sQuery(id+"F2.wireOp",EDGE,"E84");Q47=makeQuery(id+"F2.imprint","IMPRINT",FACE,{"disambiguationData":[TD([[makeQuery(id+"F2.imprint","IMPRINT",EDGE,{"derivedFrom":subQ5}),-1.0]])]});}
            var Q48;
            {var subQ0=sQuery(id+"F2.wireOp",EDGE,"E78");var subQ1=sQuery(id+"F2.wireOp",EDGE,"E75");var subQ2=makeQuery(id+"F2.imprint","INTERSECT",VERTEX,{"derivedFrom":[subQ1,subQ0]});Q48=makeQuery(id+"F2.imprint","IMPRINT",FACE,{"disambiguationData":[TD([[makeQuery(id+"F2.imprint","IMPRINT",EDGE,{"disambiguationData":[TD([[subQ2,1.0]])],"derivedFrom":subQ1}),1.0]])]});}
            var Q49;
            {var subQ0=sQuery(id+"F2.wireOp",EDGE,"E83");var subQ1=sQuery(id+"F2.wireOp",EDGE,"E75");var subQ2=makeQuery(id+"F2.imprint","INTERSECT",VERTEX,{"derivedFrom":[subQ1,subQ0]});Q49=makeQuery(id+"F2.imprint","IMPRINT",FACE,{"disambiguationData":[TD([[makeQuery(id+"F2.imprint","IMPRINT",EDGE,{"disambiguationData":[TD([[subQ2,1.0]])],"derivedFrom":subQ1}),1.0]])]});}
            var Q50;
            {var subQ5=sQuery(id+"F2.wireOp",EDGE,"E85");Q50=makeQuery(id+"F2.imprint","IMPRINT",FACE,{"disambiguationData":[TD([[makeQuery(id+"F2.imprint","IMPRINT",EDGE,{"derivedFrom":subQ5}),-1.0]])]});}
            var Q51;
            {var subQ0=sQuery(id+"F2.wireOp",EDGE,"E33");Q51=makeQuery(id+"F2.imprint","IMPRINT",FACE,{"disambiguationData":[TD([[makeQuery(id+"F2.imprint","IMPRINT",EDGE,{"derivedFrom":subQ0}),-1.0]])]});}
            var Q52;
            {var subQ0=sQuery(id+"F2.wireOp",EDGE,"E32");Q52=makeQuery(id+"F2.imprint","IMPRINT",FACE,{"disambiguationData":[TD([[makeQuery(id+"F2.imprint","IMPRINT",EDGE,{"derivedFrom":subQ0}),-1.0]])]});}
            var Q53;
            {var subQ0=sQuery(id+"F2.wireOp",EDGE,"E31");var subQ1=sQuery(id+"F2.wireOp",EDGE,"E29");var subQ2=makeQuery(id+"F2.imprint","INTERSECT",VERTEX,{"disambiguationData":[OD(1.0)],"derivedFrom":[subQ1,subQ0]});Q53=makeQuery(id+"F2.imprint","IMPRINT",FACE,{"disambiguationData":[TD([[makeQuery(id+"F2.imprint","IMPRINT",EDGE,{"disambiguationData":[TD([[subQ2,-1.0]])],"derivedFrom":subQ1}),-1.0]])]});}
            var Q54;
            {var subQ0=sQuery(id+"F2.wireOp",EDGE,"E29");var subQ1=makeQuery(id+"F2.imprint","INTERSECT",VERTEX,{"derivedFrom":[subQ0,sQuery(id+"F2.wireOp",EDGE,"E35")]});Q54=makeQuery(id+"F2.imprint","IMPRINT",FACE,{"disambiguationData":[TD([[makeQuery(id+"F2.imprint","IMPRINT",EDGE,{"disambiguationData":[TD([[subQ1,1.0]])],"derivedFrom":subQ0}),1.0]])]});}
            var Q55;
            {var subQ0=sQuery(id+"F2.wireOp",EDGE,"E35");var subQ1=sQuery(id+"F2.wireOp",EDGE,"E29");var subQ2=makeQuery(id+"F2.imprint","INTERSECT",VERTEX,{"derivedFrom":[subQ1,subQ0]});Q55=makeQuery(id+"F2.imprint","IMPRINT",FACE,{"disambiguationData":[TD([[makeQuery(id+"F2.imprint","IMPRINT",EDGE,{"disambiguationData":[TD([[subQ2,-1.0]])],"derivedFrom":subQ1}),-1.0]])]});}
            var Q56;
            {var subQ0=sQuery(id+"F2.wireOp",EDGE,"E31");var subQ1=sQuery(id+"F2.wireOp",EDGE,"E30");var subQ2=makeQuery(id+"F2.imprint","INTERSECT",VERTEX,{"disambiguationData":[OD(0.0)],"derivedFrom":[subQ1,subQ0]});Q56=makeQuery(id+"F2.imprint","IMPRINT",FACE,{"disambiguationData":[TD([[makeQuery(id+"F2.imprint","IMPRINT",EDGE,{"disambiguationData":[TD([[subQ2,-1.0]])],"derivedFrom":subQ1}),1.0]])]});}
            var Q57;
            {var subQ5=sQuery(id+"F2.wireOp",EDGE,"E36");Q57=makeQuery(id+"F2.imprint","IMPRINT",FACE,{"disambiguationData":[TD([[makeQuery(id+"F2.imprint","IMPRINT",EDGE,{"derivedFrom":subQ5}),1.0]])]});}
            var Q58;
            {var subQ5=sQuery(id+"F2.wireOp",EDGE,"E34");Q58=makeQuery(id+"F2.imprint","IMPRINT",FACE,{"disambiguationData":[TD([[makeQuery(id+"F2.imprint","IMPRINT",EDGE,{"derivedFrom":subQ5}),-1.0]])]});}
            extrude(context, id + "F3", {"entities" : qUnion([Q0, Q1, Q2, Q3, Q4, Q5, Q6, Q7, Q8, Q9, Q10, Q11, Q12, Q13, Q14, Q15, Q16, Q17, Q18, Q19, Q20, Q21, Q22, Q23, Q24, Q25, Q26, Q27, Q28, Q29, Q30, Q31, Q32, Q33, Q34, Q35, Q36, Q37, Q38, Q39, Q40, Q41, Q42, Q43, Q44, Q45, Q46, Q47, Q48, Q49, Q50, Q51, Q52, Q53, Q54, Q55, Q56, Q57, Q58]), "operationType" : NewBodyOperationType.ADD, "depth" : 2 * mm});
        }
    });
